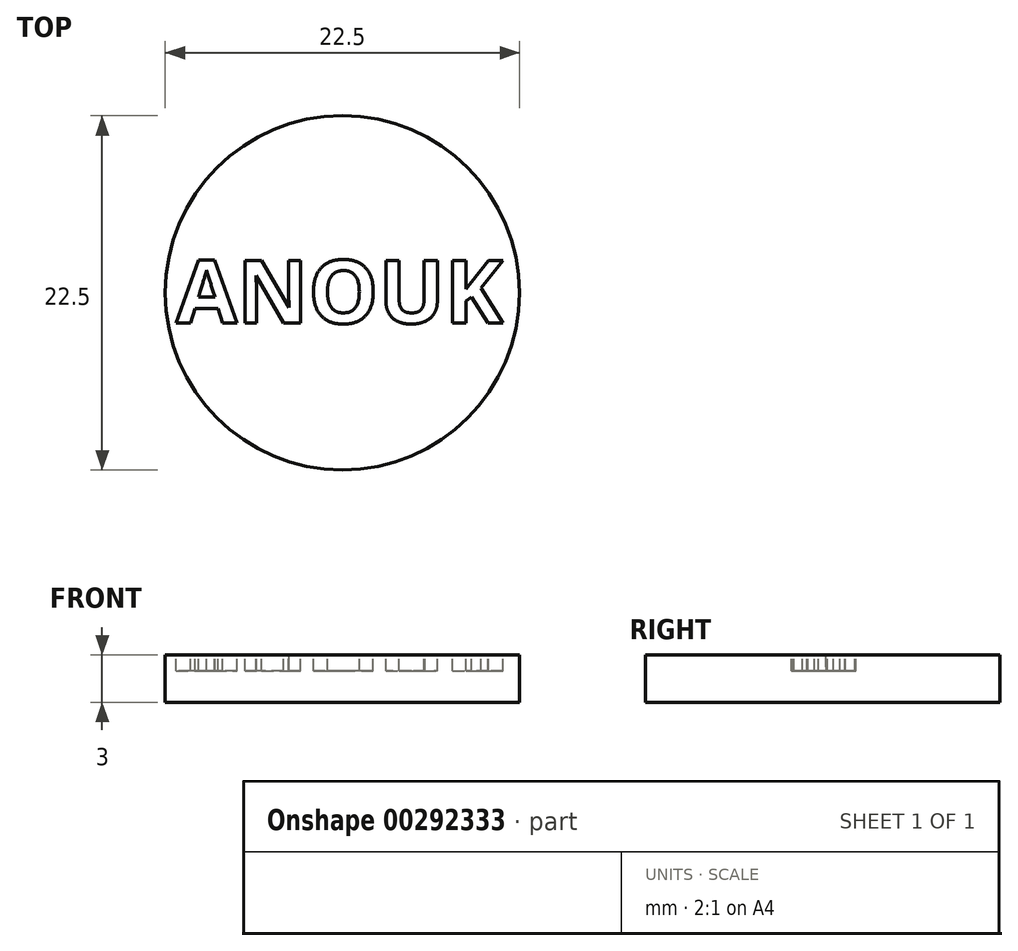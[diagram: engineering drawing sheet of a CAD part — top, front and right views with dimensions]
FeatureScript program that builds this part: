
annotation { "Feature Type Name" : "Feature", "Feature Type Description" : "" }
export const myFeature = defineFeature(function(context is Context, id is Id, definition is map)
    precondition{}
    {
        {
            var Q0;
            Q0=qCreatedBy(makeId("Top.planeOp"),FACE);
            var sketch = newSketch(context, id + "F0", { "sketchPlane" : qUnion([Q0])});
            skCircle(sketch, "E0", {"center": v(0, 0) * mm, "radius": 11.25 * mm});
            skSolve(sketch);
        }
        {
            var Q0;
            Q0=makeQuery(id+"F0.imprint","IMPRINT",FACE,{"disambiguationData":[TD([[makeQuery(id+"F0.imprint","IMPRINT",EDGE,{"derivedFrom":sQuery(id+"F0.wireOp",EDGE,"E0")}),1.0]])]});
            extrude(context, id + "F1", {"entities" : qUnion([Q0]), "depth" : 3 * mm});
        }
        {
            var Q0;
            Q0=makeQuery(id+"F1.opExtrude","CAP_FACE",FACE,{"disambiguationData":[OSD([sQuery(id+"F0.wireOp",EDGE,"E0")])],"isStart":false});
            var sketch = newSketch(context, id + "F2", { "sketchPlane" : qUnion([Q0])});
            skText(sketch, "E1", { "text": "ANOUK", "fontName": "OpenSans-Bold.ttf"});
            const initialGuessF2  = {"E1": [-0.01055, -0.00193, 1, 0, 0.00402]};
            skSetInitialGuess(sketch, initialGuessF2);
            skSolve(sketch);
        }
        {
            var Q0;
            Q0 = qSketchRegion(id + "F2", true);
            extrude(context, id + "F3", {"entities" : qUnion([Q0]), "operationType" : NewBodyOperationType.REMOVE, "oppositeDirection" : true, "depth" : 1 * mm});
        }
    });
